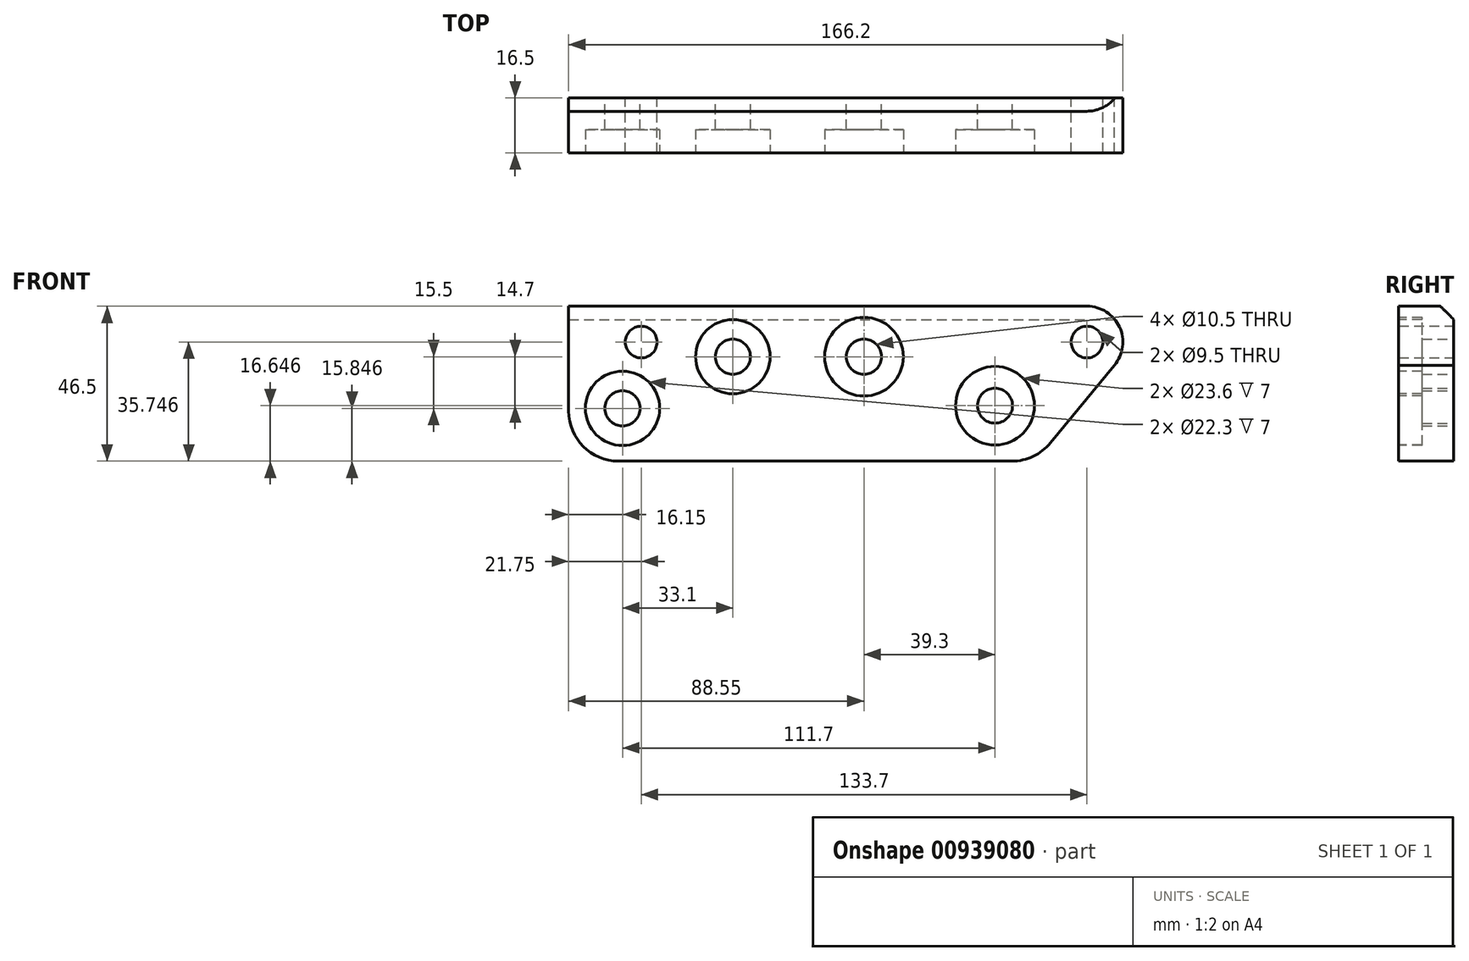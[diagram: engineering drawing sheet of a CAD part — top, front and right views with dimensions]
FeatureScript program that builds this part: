
annotation { "Feature Type Name" : "Feature", "Feature Type Description" : "" }
export const myFeature = defineFeature(function(context is Context, id is Id, definition is map)
    precondition{}
    {
        {
            var Q0;
            Q0=qCreatedBy(makeId("Front.planeOp"),FACE);
            var sketch = newSketch(context, id + "F0", { "sketchPlane" : qUnion([Q0])});
            skLineSegment(sketch, "E0.bottom", {"start": v(-111.3, 61.02) * mm, "end": v(28.7, 61.02) * mm});
            skLineSegment(sketch, "E0.top", {"start": v(-111.3, 14.52) * mm, "end": v(28.7, 14.52) * mm});
            skLineSegment(sketch, "E0.left", {"start": v(-111.3, 61.02) * mm, "end": v(-111.3, 14.52) * mm});
            skCircle(sketch, "E1", {"center": v(-95.15, 30.37) * mm, "radius": 5.25 * mm});
            skCircle(sketch, "E2", {"center": v(-89.55, 50.27) * mm, "radius": 4.75 * mm});
            skCircle(sketch, "E3", {"center": v(-62.05, 45.87) * mm, "radius": 5.25 * mm});
            skCircle(sketch, "E4", {"center": v(-22.75, 45.87) * mm, "radius": 5.25 * mm});
            skCircle(sketch, "E5", {"center": v(16.55, 31.17) * mm, "radius": 5.25 * mm});
            skCircle(sketch, "E6", {"center": v(44.15, 50.27) * mm, "radius": 4.75 * mm});
            skArc(sketch, "E7", {"start": v(52.36, 43.33) * mm, "mid": v(53.9, 54.8) * mm, "end": v(44.15, 61.02) * mm});
            skLineSegment(sketch, "E8", {"start": v(28.7, 61.02) * mm, "end": v(44.15, 61.02) * mm});
            skLineSegment(sketch, "E9", {"start": v(52.36, 43.33) * mm, "end": v(28.7, 14.52) * mm});
            skSolve(sketch);
        }
        {
            var Q0;
            Q0=makeQuery(id+"F0.imprint","IMPRINT",FACE,{"disambiguationData":[TD([[makeQuery(id+"F0.imprint","IMPRINT",EDGE,{"derivedFrom":sQuery(id+"F0.wireOp",EDGE,"E0.bottom")}),-1.0]])]});
            extrude(context, id + "F1", {"entities" : qUnion([Q0]), "depth" : 16.5 * mm, "offsetDistance" : 25 * mm});
        }
        {
            var Q0;
            Q0=makeQuery(id+"F1.opExtrude","CAP_FACE",FACE,{"disambiguationData":[OSD([sQuery(id+"F0.wireOp",EDGE,"E0.bottom"),sQuery(id+"F0.wireOp",EDGE,"E0.top"),sQuery(id+"F0.wireOp",EDGE,"E0.left"),sQuery(id+"F0.wireOp",EDGE,"E1"),sQuery(id+"F0.wireOp",EDGE,"E2"),sQuery(id+"F0.wireOp",EDGE,"E3"),sQuery(id+"F0.wireOp",EDGE,"E4"),sQuery(id+"F0.wireOp",EDGE,"E5"),sQuery(id+"F0.wireOp",EDGE,"E6"),sQuery(id+"F0.wireOp",EDGE,"E7"),sQuery(id+"F0.wireOp",EDGE,"E8"),sQuery(id+"F0.wireOp",EDGE,"E9")])],"isStart":false});
            var sketch = newSketch(context, id + "F2", { "sketchPlane" : qUnion([Q0])});
            skPoint(sketch, "E10", {"position": v(-95.15, 30.37) * mm});
            skPoint(sketch, "E11", {"position": v(-62.05, 45.87) * mm});
            skPoint(sketch, "E12", {"position": v(-22.75, 45.87) * mm});
            skPoint(sketch, "E13", {"position": v(16.55, 31.17) * mm});
            skCircle(sketch, "E14", {"center": v(-95.15, 30.37) * mm, "radius": 11.15 * mm});
            skCircle(sketch, "E15", {"center": v(-62.05, 45.87) * mm, "radius": 11.15 * mm});
            skCircle(sketch, "E16", {"center": v(-22.75, 45.87) * mm, "radius": 11.8 * mm});
            skCircle(sketch, "E17", {"center": v(16.55, 31.17) * mm, "radius": 11.8 * mm});
            skSolve(sketch);
        }
        {
            var Q0;
            Q0 = qSketchRegion(id + "F2", true);
            extrude(context, id + "F3", {"entities" : qUnion([Q0]), "operationType" : NewBodyOperationType.REMOVE, "oppositeDirection" : true, "depth" : 7 * mm, "offsetDistance" : 25 * mm});
        }
        {
            var Q0;
            Q0=makeQuery(id+"F1.opExtrude","SWEPT_EDGE",EDGE,{"disambiguationData":[OSD([sQuery(id+"F0.wireOp",EDGE,"E0.top"),sQuery(id+"F0.wireOp",EDGE,"E9")])]});
            fillet(context, id + "F4", {"entities" : qUnion([Q0]), "radius" : 15 * mm, "tangentPropagation" : true, "allowEdgeOverflow" : false});
        }
        {
            var Q0;
            Q0=makeQuery(id+"F1.opExtrude","SWEPT_EDGE",EDGE,{"disambiguationData":[OSD([sQuery(id+"F0.wireOp",EDGE,"E0.top"),sQuery(id+"F0.wireOp",EDGE,"E0.left")])]});
            fillet(context, id + "F5", {"entities" : qUnion([Q0]), "radius" : 15 * mm, "allowEdgeOverflow" : false});
        }
        {
            var Q0;
            Q0=makeQuery(id+"F1.opExtrude","CAP_EDGE",EDGE,{"disambiguationData":[OSD([sQuery(id+"F0.wireOp",EDGE,"E0.bottom"),sQuery(id+"F0.wireOp",EDGE,"E8")])],"isStart":true});
            chamfer(context, id + "F6", {"entities" : qUnion([Q0]), "width" : 4 * mm});
        }
    });
